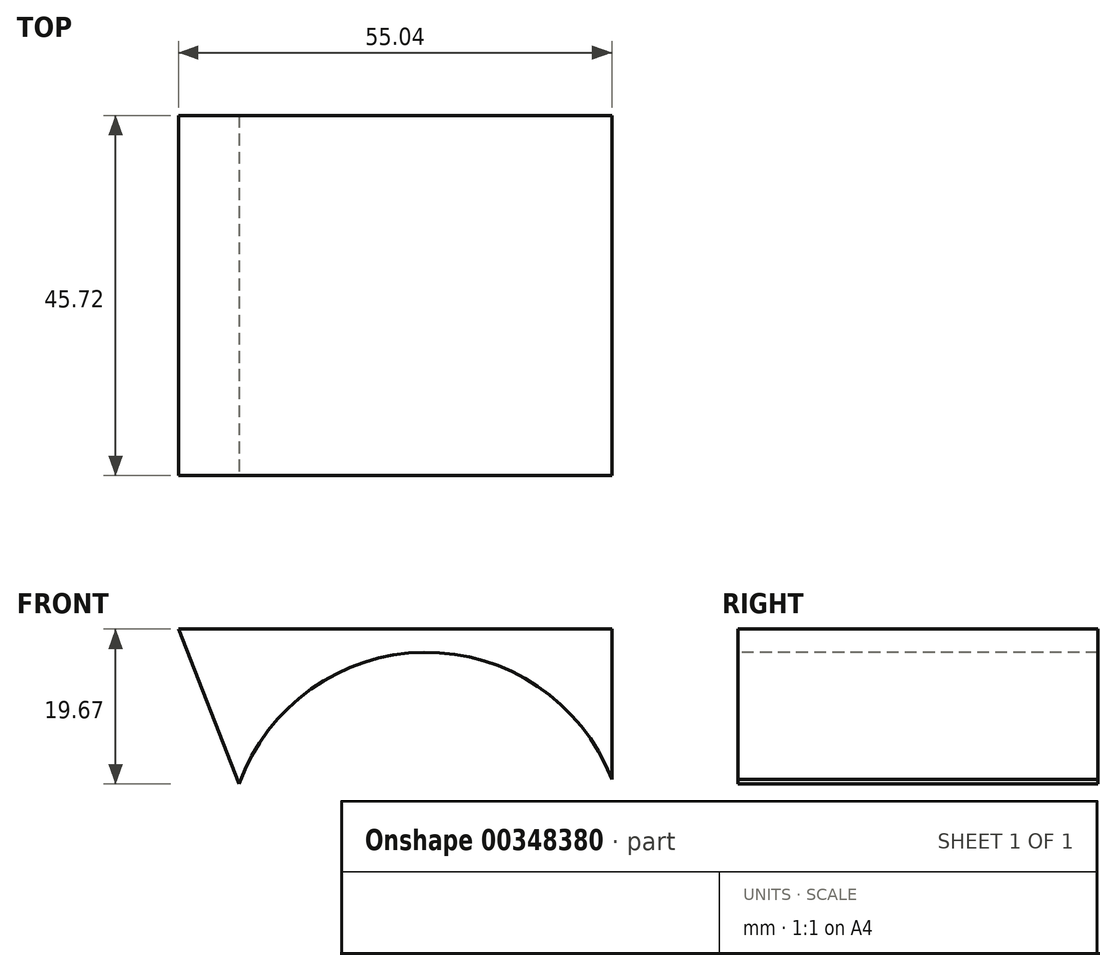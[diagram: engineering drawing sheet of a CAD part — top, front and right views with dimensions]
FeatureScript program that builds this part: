
annotation { "Feature Type Name" : "Feature", "Feature Type Description" : "" }
export const myFeature = defineFeature(function(context is Context, id is Id, definition is map)
    precondition{}
    {
        {
            var Q0;
            Q0=qCreatedBy(makeId("Front.planeOp"),FACE);
            var sketch = newSketch(context, id + "F0", { "sketchPlane" : qUnion([Q0])});
            skArc(sketch, "E0", {"start": v(14.87, -3) * mm, "mid": v(-0.1, 1.9) * mm, "end": v(-15.08, -3) * mm});
            skLineSegment(sketch, "E1.MirrorCS", {"start": v(23.45, 4.86) * mm, "end": v(23.45, -3) * mm});
            skLineSegment(sketch, "E2", {"start": v(-23.45, 4.86) * mm, "end": v(23.45, 4.86) * mm});
            skCircle(sketch, "E3", {"center": v(-0.1, -23.37) * mm, "radius": 25.27 * mm});
            skPoint(sketch, "E3.third.point", {"position": v(5.63, 1.25) * mm});
            skLineSegment(sketch, "E4", {"start": v(-31.59, 4.86) * mm, "end": v(-23.45, 4.86) * mm});
            skLineSegment(sketch, "E5", {"start": v(-31.59, 4.86) * mm, "end": v(-23.88, -14.8) * mm});
            skLineSegment(sketch, "E6", {"start": v(23.45, -3) * mm, "end": v(23.45, -14.21) * mm});
            skSolve(sketch);
        }
        {
            var Q0;
            Q0=makeQuery(id+"F0.imprint","IMPRINT",FACE,{"disambiguationData":[TD([[makeQuery(id+"F0.imprint","IMPRINT",EDGE,{"derivedFrom":sQuery(id+"F0.wireOp",EDGE,"E1.MirrorCS")}),-1.0]])]});
            extrude(context, id + "F1", {"entities" : qUnion([Q0]), "oppositeDirection" : true, "depth" : 45.72 * mm});
        }
    });
